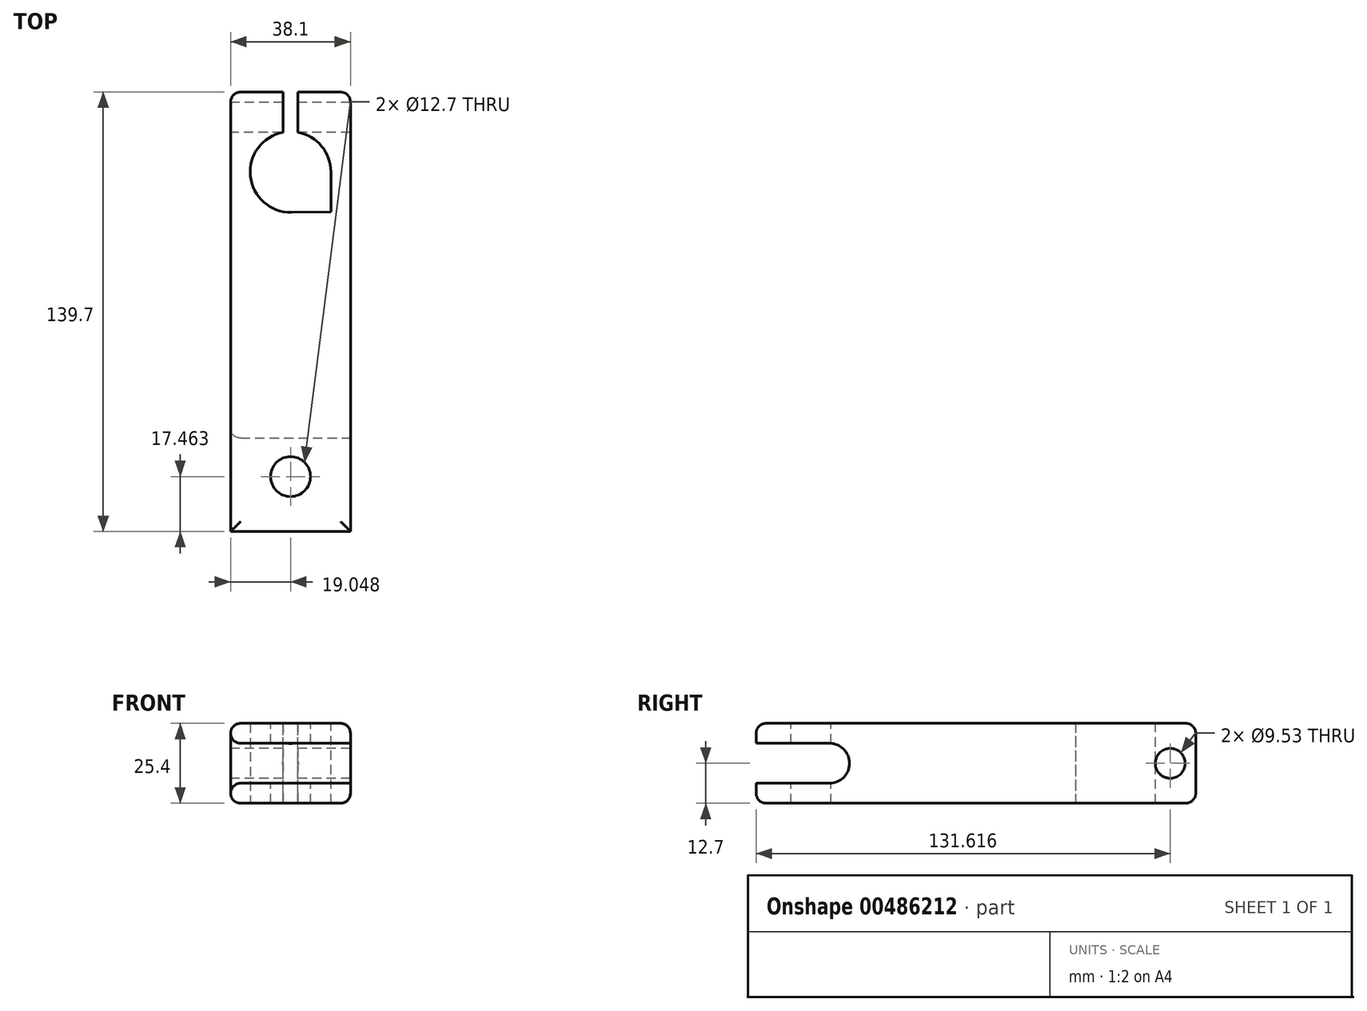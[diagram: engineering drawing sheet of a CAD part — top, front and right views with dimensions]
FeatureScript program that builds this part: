
annotation { "Feature Type Name" : "Feature", "Feature Type Description" : "" }
export const myFeature = defineFeature(function(context is Context, id is Id, definition is map)
    precondition{}
    {
        {
            var Q0;
            Q0=qCreatedBy(makeId("Top.planeOp"),FACE);
            var sketch = newSketch(context, id + "F0", { "sketchPlane" : qUnion([Q0])});
            skLineSegment(sketch, "E0", {"start": v(-32.52, 59) * mm, "end": v(5.58, 59) * mm});
            skLineSegment(sketch, "E1", {"start": v(5.58, 59) * mm, "end": v(5.58, -80.7) * mm});
            skLineSegment(sketch, "E2", {"start": v(5.58, -80.7) * mm, "end": v(-32.52, -80.7) * mm});
            skLineSegment(sketch, "E3", {"start": v(-32.52, -80.7) * mm, "end": v(-32.52, 59) * mm});
            skLineSegment(sketch, "E4", {"start": v(-32.52, 59) * mm, "end": v(-32.52, 33.6) * mm, "construction": true});
            skLineSegment(sketch, "E5", {"start": v(-32.52, 33.6) * mm, "end": v(5.58, 33.6) * mm, "construction": true});
            skLineSegment(sketch, "E6", {"start": v(5.58, 33.6) * mm, "end": v(5.58, 59) * mm, "construction": true});
            skCircle(sketch, "E7", {"center": v(-13.47, 33.6) * mm, "radius": 12.83 * mm});
            skLineSegment(sketch, "E8", {"start": v(-32.52, 59) * mm, "end": v(5.58, 59) * mm, "construction": true});
            skLineSegment(sketch, "E9", {"start": v(-32.52, 59) * mm, "end": v(-13.47, 59) * mm, "construction": true});
            skLineSegment(sketch, "E10", {"start": v(-13.47, 59) * mm, "end": v(5.58, 59) * mm, "construction": true});
            skLineSegment(sketch, "E11", {"start": v(-3.95, 59) * mm, "end": v(-13.47, 59) * mm, "construction": true});
            skLineSegment(sketch, "E12", {"start": v(-8.7, 59) * mm, "end": v(-13.47, 59) * mm, "construction": true});
            skLineSegment(sketch, "E13", {"start": v(-23, 59) * mm, "end": v(-13.47, 59) * mm, "construction": true});
            skLineSegment(sketch, "E14", {"start": v(-13.47, 59) * mm, "end": v(-18.23, 59) * mm, "construction": true});
            skPoint(sketch, "E15.endSnap0", {"position": v(5.58, 46.3) * mm});
            skSolve(sketch);
        }
        {
            var Q0;
            Q0 = qSketchRegion(id + "F0", true);
            extrude(context, id + "F1", {"entities" : qUnion([Q0]), "depth" : 25.4 * mm, "offsetDistance" : 25.4 * mm});
        }
        {
            var Q0;
            Q0=makeQuery(id+"F1.opExtrude","CAP_FACE",FACE,{"disambiguationData":[OSD([sQuery(id+"F0.wireOp",EDGE,"E0"),sQuery(id+"F0.wireOp",EDGE,"E1"),sQuery(id+"F0.wireOp",EDGE,"E2"),sQuery(id+"F0.wireOp",EDGE,"E3"),sQuery(id+"F0.wireOp",EDGE,"E7")])],"isStart":false});
            var sketch = newSketch(context, id + "F2", { "sketchPlane" : qUnion([Q0])});
            skLineSegment(sketch, "E16", {"start": v(5.58, 59) * mm, "end": v(-13.47, 59) * mm, "construction": true});
            skLineSegment(sketch, "E17", {"start": v(-32.52, 59) * mm, "end": v(-13.47, 59) * mm, "construction": true});
            skLineSegment(sketch, "E18", {"start": v(-23, 59) * mm, "end": v(-3.95, 59) * mm, "construction": true});
            skLineSegment(sketch, "E19", {"start": v(-3.95, 59) * mm, "end": v(-13.47, 59) * mm, "construction": true});
            skLineSegment(sketch, "E20", {"start": v(-23, 59) * mm, "end": v(-13.47, 59) * mm, "construction": true});
            skLineSegment(sketch, "E21", {"start": v(-18.23, 59) * mm, "end": v(-13.47, 59) * mm, "construction": true});
            skLineSegment(sketch, "E22", {"start": v(-8.7, 59) * mm, "end": v(-13.47, 59) * mm, "construction": true});
            skLineSegment(sketch, "E23", {"start": v(-11.1, 59) * mm, "end": v(-11.1, 46.2) * mm});
            skLineSegment(sketch, "E24", {"start": v(-15.85, 59) * mm, "end": v(-15.85, 46.2) * mm});
            skSolve(sketch);
        }
        {
            var Q0;
            {var subQ0=sQuery(id+"F2.wireOp",EDGE,"E23");Q0=makeQuery(id+"F2.imprint","IMPRINT",FACE,{"disambiguationData":[TD([[makeQuery(id+"F2.imprint","IMPRINT",EDGE,{"derivedFrom":subQ0}),-1.0]])]});}
            extrude(context, id + "F3", {"entities" : qUnion([Q0]), "operationType" : NewBodyOperationType.REMOVE, "oppositeDirection" : true, "depth" : 25.4 * mm, "offsetDistance" : 25.4 * mm});
        }
        {
            var Q0;
            Q0=makeQuery(id+"F1.opExtrude","SWEPT_FACE",FACE,{"disambiguationData":[OSD([sQuery(id+"F0.wireOp",EDGE,"E3")])]});
            var sketch = newSketch(context, id + "F4", { "sketchPlane" : qUnion([Q0])});
            skCircle(sketch, "E25", {"center": v(-50.92, 12.7) * mm, "radius": 4.76 * mm});
            skPoint(sketch, "E25.first.point", {"position": v(-55.68, 12.7) * mm});
            skPoint(sketch, "E25.first.point.positionSnap0", {"position": v(-59, 12.7) * mm});
            skPoint(sketch, "E25.second.point", {"position": v(-46.15, 12.7) * mm});
            skPoint(sketch, "E25.second.point.positionSnap0", {"position": v(-59, 12.7) * mm});
            skPoint(sketch, "E25.third.point", {"position": v(-53.4, 16.77) * mm});
            skSolve(sketch);
        }
        {
            var Q0;
            Q0 = qSketchRegion(id + "F4", true);
            extrude(context, id + "F5", {"entities" : qUnion([Q0]), "operationType" : NewBodyOperationType.REMOVE, "oppositeDirection" : true, "depth" : 127 * mm, "offsetDistance" : 25.4 * mm});
        }
        {
            var Q0;
            Q0=makeQuery(id+"F1.opExtrude","CAP_FACE",FACE,{"disambiguationData":[OSD([sQuery(id+"F0.wireOp",EDGE,"E0"),sQuery(id+"F0.wireOp",EDGE,"E1"),sQuery(id+"F0.wireOp",EDGE,"E2"),sQuery(id+"F0.wireOp",EDGE,"E3"),sQuery(id+"F0.wireOp",EDGE,"E7")])],"isStart":false});
            var sketch = newSketch(context, id + "F6", { "sketchPlane" : qUnion([Q0])});
            skLineSegment(sketch, "E26", {"start": v(-32.52, -10.85) * mm, "end": v(5.58, -10.85) * mm, "construction": true});
            skLineSegment(sketch, "E27", {"start": v(-13.47, -10.85) * mm, "end": v(-13.47, -80.7) * mm, "construction": true});
            skLineSegment(sketch, "E28", {"start": v(-13.47, -80.7) * mm, "end": v(-13.47, -45.77) * mm, "construction": true});
            skLineSegment(sketch, "E29", {"start": v(-13.47, -45.77) * mm, "end": v(-13.47, -63.24) * mm, "construction": true});
            skCircle(sketch, "E30", {"center": v(-13.47, -63.24) * mm, "radius": 6.35 * mm});
            skSolve(sketch);
        }
        {
            var Q0;
            Q0 = qSketchRegion(id + "F6", true);
            extrude(context, id + "F7", {"entities" : qUnion([Q0]), "operationType" : NewBodyOperationType.REMOVE, "oppositeDirection" : true, "depth" : 50.8 * mm, "offsetDistance" : 25.4 * mm});
        }
        {
            var Q0;
            Q0=makeQuery(id+"F1.opExtrude","SWEPT_FACE",FACE,{"disambiguationData":[OSD([sQuery(id+"F0.wireOp",EDGE,"E1")])]});
            var sketch = newSketch(context, id + "F8", { "sketchPlane" : qUnion([Q0])});
            skLineSegment(sketch, "E31", {"start": v(-80.7, 25.4) * mm, "end": v(-80.7, 12.7) * mm, "construction": true});
            skLineSegment(sketch, "E32", {"start": v(-80.7, 12.7) * mm, "end": v(-80.7, 0) * mm, "construction": true});
            skLineSegment(sketch, "E33", {"start": v(-80.7, 6.35) * mm, "end": v(-57.36, 6.35) * mm});
            skLineSegment(sketch, "E34", {"start": v(-57.36, 6.35) * mm, "end": v(-57.36, 19.05) * mm});
            skPoint(sketch, "E34.endSnap0", {"position": v(-80.7, 19.05) * mm});
            skLineSegment(sketch, "E35", {"start": v(-57.36, 19.05) * mm, "end": v(-80.7, 19.05) * mm});
            skLineSegment(sketch, "E36", {"start": v(-80.7, 6.35) * mm, "end": v(-80.7, 19.05) * mm});
            skArc(sketch, "E37", {"start": v(-57.36, 6.35) * mm, "mid": v(-51, 12.7) * mm, "end": v(-57.36, 19.05) * mm});
            skSolve(sketch);
        }
        {
            var Q0;
            Q0 = qSketchRegion(id + "F8", true);
            extrude(context, id + "F9", {"entities" : qUnion([Q0]), "operationType" : NewBodyOperationType.REMOVE, "oppositeDirection" : true, "depth" : 76.2 * mm, "offsetDistance" : 25.4 * mm});
        }
        {
            var Q0;
            Q0=makeQuery(id+"F9.boolean.opBoolean","COPY",EDGE,{"derivedFrom":makeQuery(id+"F9.opExtrude","CAP_EDGE",EDGE,{"disambiguationData":[OSD([sQuery(id+"F8.wireOp",EDGE,"E35")])],"isStart":true})});
            var Q1;
            Q1=makeQuery(id+"F9.boolean.opBoolean","COPY",EDGE,{"derivedFrom":makeQuery(id+"F9.opExtrude","SWEPT_EDGE",EDGE,{"disambiguationData":[OSD([sQuery(id+"F0.wireOp",EDGE,"E1"),sQuery(id+"F0.wireOp",EDGE,"E2"),sQuery(id+"F8.wireOp",EDGE,"E33"),sQuery(id+"F8.wireOp",EDGE,"E36")])]})});
            var Q2;
            Q2=makeQuery(id+"F1.opExtrude","CAP_EDGE",EDGE,{"disambiguationData":[OSD([sQuery(id+"F0.wireOp",EDGE,"E1")])],"isStart":false});
            var Q3;
            Q3=makeQuery(id+"F1.opExtrude","CAP_EDGE",EDGE,{"disambiguationData":[OSD([sQuery(id+"F0.wireOp",EDGE,"E3")])],"isStart":false});
            var Q4;
            Q4=makeQuery(id+"F1.opExtrude","CAP_EDGE",EDGE,{"disambiguationData":[OSD([sQuery(id+"F0.wireOp",EDGE,"E2")])],"isStart":false});
            var Q5;
            Q5=makeQuery(id+"F1.opExtrude","CAP_EDGE",EDGE,{"disambiguationData":[OSD([sQuery(id+"F0.wireOp",EDGE,"E1")])],"isStart":true});
            var Q6;
            Q6=makeQuery(id+"F1.opExtrude","CAP_EDGE",EDGE,{"disambiguationData":[OSD([sQuery(id+"F0.wireOp",EDGE,"E2")])],"isStart":true});
            var Q7;
            {var subQ0=sQuery(id+"F0.wireOp",EDGE,"E0");var subQ1=sQuery(id+"F0.wireOp",EDGE,"E3");Q7=makeQuery(id+"F3.boolean.opBoolean","SPLIT",EDGE,{"disambiguationData":[TD([makeQuery(id+"F1.opExtrude","SWEPT_FACE",FACE,{"disambiguationData":[OSD([subQ1])]})])],"derivedFrom":makeQuery(id+"F1.opExtrude","CAP_EDGE",EDGE,{"disambiguationData":[OSD([subQ0])],"isStart":false})});}
            var Q8;
            {var subQ0=sQuery(id+"F0.wireOp",EDGE,"E0");var subQ1=sQuery(id+"F0.wireOp",EDGE,"E1");Q8=makeQuery(id+"F3.boolean.opBoolean","SPLIT",EDGE,{"disambiguationData":[TD([makeQuery(id+"F1.opExtrude","SWEPT_FACE",FACE,{"disambiguationData":[OSD([subQ1])]})])],"derivedFrom":makeQuery(id+"F1.opExtrude","CAP_EDGE",EDGE,{"disambiguationData":[OSD([subQ0])],"isStart":false})});}
            var Q9;
            Q9=makeQuery(id+"F1.opExtrude","SWEPT_EDGE",EDGE,{"disambiguationData":[OSD([sQuery(id+"F0.wireOp",EDGE,"E0"),sQuery(id+"F0.wireOp",EDGE,"E3")])]});
            var Q10;
            Q10=makeQuery(id+"F1.opExtrude","SWEPT_EDGE",EDGE,{"disambiguationData":[OSD([sQuery(id+"F0.wireOp",EDGE,"E0"),sQuery(id+"F0.wireOp",EDGE,"E1")])]});
            var Q11;
            {var subQ0=sQuery(id+"F0.wireOp",EDGE,"E0");var subQ1=sQuery(id+"F0.wireOp",EDGE,"E1");Q11=makeQuery(id+"F3.boolean.opBoolean","SPLIT",EDGE,{"disambiguationData":[TD([makeQuery(id+"F1.opExtrude","SWEPT_FACE",FACE,{"disambiguationData":[OSD([subQ1])]})])],"derivedFrom":makeQuery(id+"F1.opExtrude","CAP_EDGE",EDGE,{"disambiguationData":[OSD([subQ0])],"isStart":true})});}
            var Q12;
            {var subQ0=sQuery(id+"F0.wireOp",EDGE,"E0");var subQ1=sQuery(id+"F0.wireOp",EDGE,"E3");Q12=makeQuery(id+"F3.boolean.opBoolean","SPLIT",EDGE,{"disambiguationData":[TD([makeQuery(id+"F1.opExtrude","SWEPT_FACE",FACE,{"disambiguationData":[OSD([subQ1])]})])],"derivedFrom":makeQuery(id+"F1.opExtrude","CAP_EDGE",EDGE,{"disambiguationData":[OSD([subQ0])],"isStart":true})});}
            var Q13;
            Q13=makeQuery(id+"F1.opExtrude","CAP_EDGE",EDGE,{"disambiguationData":[OSD([sQuery(id+"F0.wireOp",EDGE,"E3")])],"isStart":true});
            var Q14;
            Q14=makeQuery(id+"F9.boolean.opBoolean","COPY",EDGE,{"derivedFrom":makeQuery(id+"F9.opExtrude","SWEPT_EDGE",EDGE,{"disambiguationData":[OSD([sQuery(id+"F0.wireOp",EDGE,"E1"),sQuery(id+"F0.wireOp",EDGE,"E2"),sQuery(id+"F8.wireOp",EDGE,"E35"),sQuery(id+"F8.wireOp",EDGE,"E36")])]})});
            var Q15;
            Q15=makeQuery(id+"F9.boolean.opBoolean","INTERSECT",EDGE,{"derivedFrom":[makeQuery(id+"F1.opExtrude","SWEPT_FACE",FACE,{"disambiguationData":[OSD([sQuery(id+"F0.wireOp",EDGE,"E3")])]}),makeQuery(id+"F9.opExtrude","SWEPT_FACE",FACE,{"disambiguationData":[OSD([sQuery(id+"F8.wireOp",EDGE,"E37")])]})]});
            var Q16;
            Q16=makeQuery(id+"F9.boolean.opBoolean","INTERSECT",EDGE,{"derivedFrom":[makeQuery(id+"F1.opExtrude","SWEPT_FACE",FACE,{"disambiguationData":[OSD([sQuery(id+"F0.wireOp",EDGE,"E3")])]}),makeQuery(id+"F9.opExtrude","SWEPT_FACE",FACE,{"disambiguationData":[OSD([sQuery(id+"F8.wireOp",EDGE,"E33")])]})]});
            var Q17;
            Q17=makeQuery(id+"F9.boolean.opBoolean","INTERSECT",EDGE,{"derivedFrom":[makeQuery(id+"F1.opExtrude","SWEPT_FACE",FACE,{"disambiguationData":[OSD([sQuery(id+"F0.wireOp",EDGE,"E3")])]}),makeQuery(id+"F9.opExtrude","SWEPT_FACE",FACE,{"disambiguationData":[OSD([sQuery(id+"F8.wireOp",EDGE,"E35")])]})]});
            fillet(context, id + "F10", {"entities" : qUnion([Q0, Q1, Q2, Q3, Q4, Q5, Q6, Q7, Q8, Q9, Q10, Q11, Q12, Q13, Q14, Q15, Q16, Q17]), "radius" : 3.17 * mm, "tangentPropagation" : true, "allowEdgeOverflow" : false});
        }
        {
            var Q0;
            Q0=makeQuery(id+"F1.opExtrude","CAP_FACE",FACE,{"disambiguationData":[OSD([sQuery(id+"F0.wireOp",EDGE,"E0"),sQuery(id+"F0.wireOp",EDGE,"E1"),sQuery(id+"F0.wireOp",EDGE,"E2"),sQuery(id+"F0.wireOp",EDGE,"E3"),sQuery(id+"F0.wireOp",EDGE,"E7")])],"isStart":false});
            var sketch = newSketch(context, id + "F11", { "sketchPlane" : qUnion([Q0])});
            skLineSegment(sketch, "E38", {"start": v(-13.47, 33.6) * mm, "end": v(-0.65, 33.6) * mm, "construction": true});
            skLineSegment(sketch, "E39", {"start": v(-0.65, 33.6) * mm, "end": v(-0.65, 20.9) * mm});
            skLineSegment(sketch, "E40", {"start": v(-13.47, 33.6) * mm, "end": v(-13.47, 20.77) * mm, "construction": true});
            skLineSegment(sketch, "E41", {"start": v(-13.47, 20.77) * mm, "end": v(-0.65, 20.9) * mm});
            skSolve(sketch);
        }
        {
            var Q0;
            {var subQ0=sQuery(id+"F11.wireOp",EDGE,"E39");Q0=makeQuery(id+"F11.imprint","IMPRINT",FACE,{"disambiguationData":[TD([[makeQuery(id+"F11.imprint","IMPRINT",EDGE,{"derivedFrom":subQ0}),-1.0]])]});}
            extrude(context, id + "F12", {"entities" : qUnion([Q0]), "operationType" : NewBodyOperationType.REMOVE, "oppositeDirection" : true, "depth" : 25.4 * mm, "offsetDistance" : 25.4 * mm});
        }
    });
